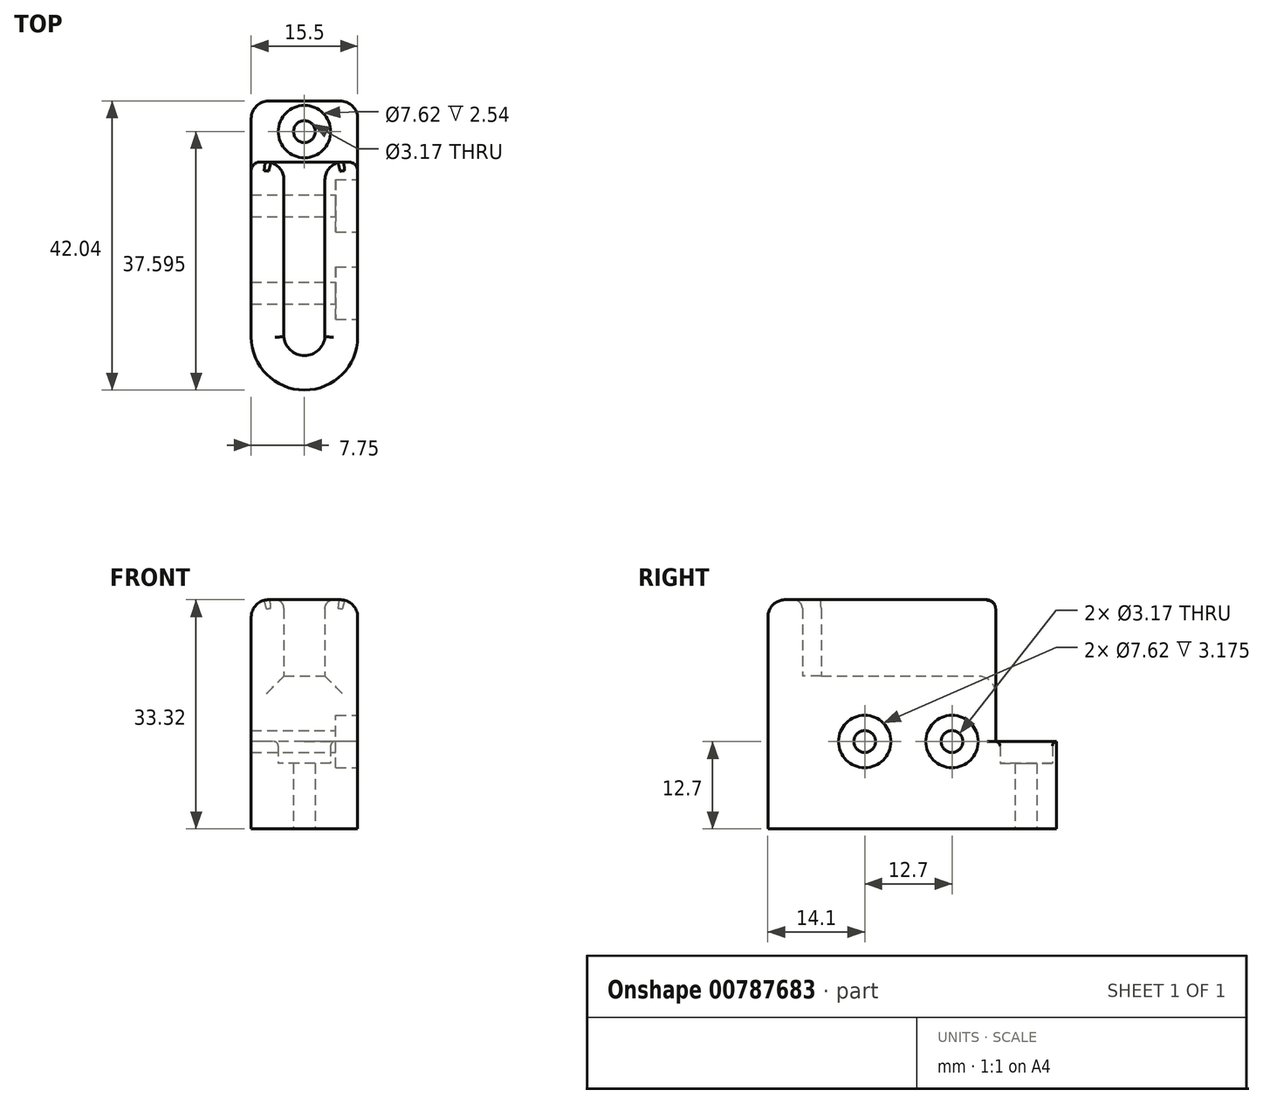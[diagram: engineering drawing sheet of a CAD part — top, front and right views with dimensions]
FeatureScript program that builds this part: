
annotation { "Feature Type Name" : "Feature", "Feature Type Description" : "" }
export const myFeature = defineFeature(function(context is Context, id is Id, definition is map)
    precondition{}
    {
        {
            var Q0;
            Q0=qCreatedBy(makeId("Top.planeOp"),FACE);
            var sketch = newSketch(context, id + "F0", { "sketchPlane" : qUnion([Q0])});
            skLineSegment(sketch, "E0", {"start": v(2.98, 0) * mm, "end": v(2.98, 25.4) * mm});
            skLineSegment(sketch, "E1", {"start": v(-2.98, 25.4) * mm, "end": v(2.98, 25.4) * mm});
            skLineSegment(sketch, "E2", {"start": v(-2.98, 25.4) * mm, "end": v(-2.98, 0) * mm});
            skLineSegment(sketch, "E3", {"start": v(2.98, 25.4) * mm, "end": v(7.75, 25.4) * mm});
            skLineSegment(sketch, "E4", {"start": v(7.75, 25.4) * mm, "end": v(7.75, 0) * mm});
            skLineSegment(sketch, "E5", {"start": v(-2.98, 25.4) * mm, "end": v(-7.75, 25.4) * mm});
            skLineSegment(sketch, "E6", {"start": v(-7.75, 0) * mm, "end": v(-7.75, 25.4) * mm});
            skArc(sketch, "E7", {"start": v(-2.98, 0) * mm, "mid": v(0, -2.98) * mm, "end": v(2.98, 0) * mm});
            skLineSegment(sketch, "E8", {"start": v(-2.98, 0) * mm, "end": v(-7.75, 0) * mm});
            skLineSegment(sketch, "E9", {"start": v(7.75, 0) * mm, "end": v(2.98, 0) * mm});
            skArc(sketch, "E10", {"start": v(-7.75, 0) * mm, "mid": v(0, -7.75) * mm, "end": v(7.75, 0) * mm});
            skLineSegment(sketch, "E11", {"start": v(-7.75, 25.4) * mm, "end": v(-7.75, 34.3) * mm});
            skLineSegment(sketch, "E12", {"start": v(7.75, 25.4) * mm, "end": v(7.75, 34.3) * mm});
            skLineSegment(sketch, "E13", {"start": v(7.75, 34.3) * mm, "end": v(-7.75, 34.3) * mm});
            skCircle(sketch, "E14", {"center": v(0, 29.85) * mm, "radius": 1.59 * mm});
            skCircle(sketch, "E15", {"center": v(0, 29.85) * mm, "radius": 3.81 * mm});
            skSolve(sketch);
        }
        {
            var Q0;
            Q0=makeQuery(id+"F0.imprint","IMPRINT",FACE,{"disambiguationData":[TD([[makeQuery(id+"F0.imprint","IMPRINT",EDGE,{"derivedFrom":sQuery(id+"F0.wireOp",EDGE,"E0")}),-1.0]])]});
            var Q1;
            {var subQ0=sQuery(id+"F0.wireOp",EDGE,"E0");Q1=makeQuery(id+"F0.imprint","IMPRINT",FACE,{"disambiguationData":[TD([[makeQuery(id+"F0.imprint","IMPRINT",EDGE,{"derivedFrom":subQ0}),1.0]])]});}
            var Q2;
            Q2=makeQuery(id+"F0.imprint","IMPRINT",FACE,{"disambiguationData":[TD([[makeQuery(id+"F0.imprint","IMPRINT",EDGE,{"derivedFrom":sQuery(id+"F0.wireOp",EDGE,"E2")}),-1.0]])]});
            var Q3;
            {var subQ0=sQuery(id+"F0.wireOp",EDGE,"E8");Q3=makeQuery(id+"F0.imprint","IMPRINT",FACE,{"disambiguationData":[TD([[makeQuery(id+"F0.imprint","IMPRINT",EDGE,{"derivedFrom":subQ0}),1.0]])]});}
            var Q4;
            Q4=makeQuery(id+"F0.imprint","IMPRINT",FACE,{"disambiguationData":[TD([[makeQuery(id+"F0.imprint","IMPRINT",EDGE,{"derivedFrom":sQuery(id+"F0.wireOp",EDGE,"AUI6VbHG-UpWO-e9Ka-JriX-rNekk1wkd0BI")}),-1.0]])]});
            extrude(context, id + "F1", {"entities" : qUnion([Q0, Q1, Q2, Q3, Q4]), "depth" : 22.21 * mm, "offsetDistance" : 25.4 * mm});
        }
        {
            var Q0;
            Q0=makeQuery(id+"F0.imprint","IMPRINT",FACE,{"disambiguationData":[TD([[makeQuery(id+"F0.imprint","IMPRINT",EDGE,{"derivedFrom":sQuery(id+"F0.wireOp",EDGE,"E1")}),1.0]])]});
            extrude(context, id + "F2", {"entities" : qUnion([Q0]), "operationType" : NewBodyOperationType.ADD, "depth" : 12.7 * mm, "offsetDistance" : 25.4 * mm});
        }
        {
            var Q0;
            Q0=makeQuery(id+"F1.opExtrude","CAP_FACE",FACE,{"disambiguationData":[OSD([sQuery(id+"F0.wireOp",EDGE,"E1"),sQuery(id+"F0.wireOp",EDGE,"E3"),sQuery(id+"F0.wireOp",EDGE,"E4"),sQuery(id+"F0.wireOp",EDGE,"E5"),sQuery(id+"F0.wireOp",EDGE,"E6"),sQuery(id+"F0.wireOp",EDGE,"E10"),sQuery(id+"F0.wireOp",EDGE,"AUI6VbHG-UpWO-e9Ka-JriX-rNekk1wkd0BI")])],"isStart":false});
            var sketch = newSketch(context, id + "F3", { "sketchPlane" : qUnion([Q0])});
            skLineSegment(sketch, "E16.0", {"start": v(-2.98, 25.4) * mm, "end": v(-2.98, 0) * mm});
            skLineSegment(sketch, "E16.1", {"start": v(2.98, 0) * mm, "end": v(2.98, 25.4) * mm});
            skLineSegment(sketch, "E16.3", {"start": v(-2.98, 25.4) * mm, "end": v(2.98, 25.4) * mm});
            skArc(sketch, "E17", {"start": v(-2.98, 0) * mm, "mid": v(0, -2.72) * mm, "end": v(2.98, 0) * mm});
            skSolve(sketch);
        }
        {
            var Q0;
            {var subQ1=sQuery(id+"F3.wireOp",EDGE,"E16.0");Q0=makeQuery(id+"F3.imprint","IMPRINT",FACE,{"disambiguationData":[TD([[makeQuery(id+"F3.imprint","IMPRINT",EDGE,{"derivedFrom":subQ1}),-1.0]])]});}
            extrude(context, id + "F4", {"entities" : qUnion([Q0]), "operationType" : NewBodyOperationType.ADD, "depth" : 11.1 * mm, "offsetDistance" : 25.4 * mm});
        }
        {
            var Q0;
            Q0=makeQuery(id+"F4.opExtrude","CAP_EDGE",EDGE,{"disambiguationData":[OSD([sQuery(id+"F0.wireOp",EDGE,"E6")])],"isStart":false});
            fillet(context, id + "F5", {"entities" : qUnion([Q0]), "radius" : 2.54 * mm, "tangentPropagation" : true, "allowEdgeOverflow" : false});
        }
        {
            var Q0;
            Q0=makeQuery(id+"F4.opExtrude","SWEPT_EDGE",EDGE,{"disambiguationData":[OSD([sQuery(id+"F0.wireOp",EDGE,"E1"),sQuery(id+"F0.wireOp",EDGE,"E3"),sQuery(id+"F0.wireOp",EDGE,"E5"),sQuery(id+"F3.wireOp",EDGE,"E16.1"),sQuery(id+"F3.wireOp",EDGE,"E16.3")])]});
            var Q1;
            Q1=makeQuery(id+"F4.opExtrude","SWEPT_EDGE",EDGE,{"disambiguationData":[OSD([sQuery(id+"F0.wireOp",EDGE,"E1"),sQuery(id+"F0.wireOp",EDGE,"E3"),sQuery(id+"F0.wireOp",EDGE,"E5"),sQuery(id+"F3.wireOp",EDGE,"E16.0"),sQuery(id+"F3.wireOp",EDGE,"E16.3")])]});
            var Q2;
            Q2=makeQuery(id+"F1.opExtrude","CAP_EDGE",EDGE,{"disambiguationData":[OSD([sQuery(id+"F0.wireOp",EDGE,"E1"),sQuery(id+"F0.wireOp",EDGE,"E3"),sQuery(id+"F0.wireOp",EDGE,"E5")])],"isStart":false});
            fillet(context, id + "F6", {"entities" : qUnion([Q0, Q1, Q2]), "radius" : 2.54 * mm, "tangentPropagation" : true, "allowEdgeOverflow" : false});
        }
        {
            var Q0;
            {var subQ0=sQuery(id+"F0.wireOp",EDGE,"E6");var subQ1=sQuery(id+"F0.wireOp",EDGE,"E5");Q0=makeQuery(id+"F4.boolean.opBoolean","MERGE",EDGE,{"derivedFrom":[makeQuery(id+"F1.opExtrude","SWEPT_EDGE",EDGE,{"disambiguationData":[OSD([subQ1,subQ0,sQuery(id+"F0.wireOp",EDGE,"E11")])]}),makeQuery(id+"F4.opExtrude","SWEPT_EDGE",EDGE,{"disambiguationData":[OSD([sQuery(id+"F0.wireOp",EDGE,"E1"),sQuery(id+"F0.wireOp",EDGE,"E3"),subQ1,subQ0])]})]});}
            var Q1;
            {var subQ0=sQuery(id+"F0.wireOp",EDGE,"E4");var subQ1=sQuery(id+"F0.wireOp",EDGE,"E3");Q1=makeQuery(id+"F4.boolean.opBoolean","MERGE",EDGE,{"derivedFrom":[makeQuery(id+"F1.opExtrude","SWEPT_EDGE",EDGE,{"disambiguationData":[OSD([subQ1,subQ0,sQuery(id+"F0.wireOp",EDGE,"E12")])]}),makeQuery(id+"F4.opExtrude","SWEPT_EDGE",EDGE,{"disambiguationData":[OSD([sQuery(id+"F0.wireOp",EDGE,"E1"),subQ1,subQ0,sQuery(id+"F0.wireOp",EDGE,"E5")])]})]});}
            var Q2;
            Q2=makeQuery(id+"F4.opExtrude","CAP_EDGE",EDGE,{"disambiguationData":[OSD([sQuery(id+"F3.wireOp",EDGE,"E16.1")])],"isStart":false});
            var Q3;
            Q3=makeQuery(id+"F4.opExtrude","CAP_EDGE",EDGE,{"disambiguationData":[OSD([sQuery(id+"F3.wireOp",EDGE,"E16.0")])],"isStart":false});
            var Q4;
            Q4=makeQuery(id+"F4.opExtrude","CAP_EDGE",EDGE,{"disambiguationData":[OSD([sQuery(id+"F3.wireOp",EDGE,"E17")])],"isStart":false});
            fillet(context, id + "F7", {"entities" : qUnion([Q0, Q1, Q2, Q3, Q4]), "radius" : 1.27 * mm, "tangentPropagation" : true, "allowEdgeOverflow" : false});
        }
        {
            var Q0;
            Q0=makeQuery(id+"F2.opExtrude","SWEPT_EDGE",EDGE,{"disambiguationData":[OSD([sQuery(id+"F0.wireOp",EDGE,"E11"),sQuery(id+"F0.wireOp",EDGE,"E13")])]});
            var Q1;
            Q1=makeQuery(id+"F2.opExtrude","SWEPT_EDGE",EDGE,{"disambiguationData":[OSD([sQuery(id+"F0.wireOp",EDGE,"E12"),sQuery(id+"F0.wireOp",EDGE,"E13")])]});
            fillet(context, id + "F8", {"entities" : qUnion([Q0, Q1]), "radius" : 2.54 * mm, "tangentPropagation" : true, "allowEdgeOverflow" : false});
        }
        {
            var Q0;
            {var subQ0=sQuery(id+"F0.wireOp",EDGE,"E4");Q0=makeQuery(id+"F4.boolean.opBoolean","MERGE",FACE,{"derivedFrom":[makeQuery(id+"F2.boolean.opBoolean","MERGE",FACE,{"derivedFrom":[makeQuery(id+"F1.opExtrude","SWEPT_FACE",FACE,{"disambiguationData":[OSD([subQ0])]}),makeQuery(id+"F2.opExtrude","SWEPT_FACE",FACE,{"disambiguationData":[OSD([sQuery(id+"F0.wireOp",EDGE,"E12")])]})]}),makeQuery(id+"F4.opExtrude","SWEPT_FACE",FACE,{"disambiguationData":[OSD([subQ0])]})]});}
            var sketch = newSketch(context, id + "F9", { "sketchPlane" : qUnion([Q0])});
            skLineSegment(sketch, "E18", {"start": v(0, 0) * mm, "end": v(6.35, 0) * mm});
            skLineSegment(sketch, "E19", {"start": v(6.35, 0) * mm, "end": v(6.35, 12.7) * mm});
            skCircle(sketch, "E20", {"center": v(6.35, 12.7) * mm, "radius": 1.59 * mm});
            skCircle(sketch, "E21", {"center": v(6.35, 12.7) * mm, "radius": 3.81 * mm});
            skLineSegment(sketch, "E22", {"start": v(6.35, 0) * mm, "end": v(19.05, 0) * mm});
            skLineSegment(sketch, "E23", {"start": v(19.05, 12.7) * mm, "end": v(19.05, 0) * mm});
            skCircle(sketch, "E24", {"center": v(19.05, 12.7) * mm, "radius": 1.59 * mm});
            skCircle(sketch, "E25", {"center": v(19.05, 12.7) * mm, "radius": 3.81 * mm});
            skSolve(sketch);
        }
        {
            var Q0;
            Q0=makeQuery(id+"F9.imprint","IMPRINT",FACE,{"disambiguationData":[TD([[makeQuery(id+"F9.imprint","IMPRINT",EDGE,{"derivedFrom":sQuery(id+"F9.wireOp",EDGE,"E20")}),1.0]])]});
            var Q1;
            Q1=makeQuery(id+"F9.imprint","IMPRINT",FACE,{"disambiguationData":[TD([[makeQuery(id+"F9.imprint","IMPRINT",EDGE,{"derivedFrom":sQuery(id+"F9.wireOp",EDGE,"E24")}),1.0]])]});
            extrude(context, id + "F10", {"entities" : qUnion([Q0, Q1]), "operationType" : NewBodyOperationType.REMOVE, "endBound" : BoundingType.THROUGH_ALL, "oppositeDirection" : true, "depth" : 25.4 * mm, "offsetDistance" : 25.4 * mm});
        }
        {
            var Q0;
            Q0=makeQuery(id+"F9.imprint","IMPRINT",FACE,{"disambiguationData":[TD([[makeQuery(id+"F9.imprint","IMPRINT",EDGE,{"derivedFrom":sQuery(id+"F9.wireOp",EDGE,"E20")}),-1.0]])]});
            var Q1;
            Q1=makeQuery(id+"F9.imprint","IMPRINT",FACE,{"disambiguationData":[TD([[makeQuery(id+"F9.imprint","IMPRINT",EDGE,{"derivedFrom":sQuery(id+"F9.wireOp",EDGE,"E24")}),-1.0]])]});
            extrude(context, id + "F11", {"entities" : qUnion([Q0, Q1]), "operationType" : NewBodyOperationType.REMOVE, "oppositeDirection" : true, "depth" : 3.17 * mm, "offsetDistance" : 25.4 * mm});
        }
        {
            var Q0;
            Q0=makeQuery(id+"F0.imprint","IMPRINT",FACE,{"disambiguationData":[TD([[makeQuery(id+"F0.imprint","IMPRINT",EDGE,{"derivedFrom":sQuery(id+"F0.wireOp",EDGE,"E14")}),-1.0]])]});
            extrude(context, id + "F12", {"entities" : qUnion([Q0]), "operationType" : NewBodyOperationType.ADD, "depth" : 9.52 * mm, "offsetDistance" : 25.4 * mm});
        }
        {
            var Q0;
            Q0=makeQuery(id+"F11.boolean.opBoolean","COPY",EDGE,{"derivedFrom":makeQuery(id+"F11.opExtrude","CAP_EDGE",EDGE,{"disambiguationData":[OSD([sQuery(id+"F9.wireOp",EDGE,"E21")])],"isStart":true})});
            var Q1;
            Q1=makeQuery(id+"F2.opExtrude","CAP_EDGE",EDGE,{"disambiguationData":[OSD([sQuery(id+"F0.wireOp",EDGE,"E15")])],"isStart":false});
            var Q2;
            Q2=makeQuery(id+"F11.boolean.opBoolean","COPY",EDGE,{"derivedFrom":makeQuery(id+"F11.opExtrude","CAP_EDGE",EDGE,{"disambiguationData":[OSD([sQuery(id+"F9.wireOp",EDGE,"E25")])],"isStart":true})});
            fillet(context, id + "F13", {"entities" : qUnion([Q0, Q1, Q2]), "radius" : 0.64 * mm, "tangentPropagation" : true, "allowEdgeOverflow" : false});
        }
    });
